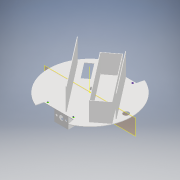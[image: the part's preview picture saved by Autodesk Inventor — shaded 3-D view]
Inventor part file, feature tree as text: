
AUTODESK INVENTOR PART (.ipt)
format: ipt  version: 2020 (Build 240168000, 168)  size: 422,400 bytes
history: native  units: mm
features: sketch x20, extrude x16, reference x13, other x3, fillet x3, projected_geometry x2, plane x1, mirror x1
ambient origin geometry x8: Origin, YZ Plane, XZ Plane, XY Plane, X Axis, Y Axis, Z Axis, Center Point
bodies: Solid1 (feature_tree)
feature tree (59):
  extrude  "Extrusion1"  Depth=1.0mm TaperAngle=0.0deg
  sketch  "Sketch2"  dims[d5=1.0mm d6=0.0mm d29=12.5mm]
  extrude  "Extrusion2"  Depth=12.5mm
  extrude  "Extrusion6"  Depth=1.0mm
  extrude  "Extrusion7"  Depth=25.0mm
  extrude  "Extrusion8"  Depth=1.0mm TaperAngle=0.0deg
  plane  "Work Plane1"
  mirror  "Mirror1"
  extrude  "Extrusion9"  Depth=1.0mm
  extrude  "Extrusion10"  Depth=40.0mm TaperAngle=0.0deg
  extrude  "Extrusion11"  Depth=24.0mm
  extrude  "Extrusion13"  Depth=34.0mm TaperAngle=0.0deg
  other  "Work Axis1"
  extrude  "Extrusion15"  Depth=4.0mm TaperAngle=0.0deg
  fillet  "Fillet2"  Radius=1.0mm
  extrude  "Extrusion21"  Depth=1.0mm TaperAngle=0.0deg
  extrude  "Extrusion24"  Depth=1.0mm
  extrude  "Extrusion25"  Depth=1.0mm
  sketch  "Sketch30"  dims[d105=2.0mm d106=1.0mm d107=0.0mm]
  sketch  "Sketch31"  dims[d111=1.0mm d112=0.0mm d113=2.0mm d114=1.0mm d115=0.0mm]
  extrude  "Extrusion27"  Depth=40.0mm TaperAngle=0.0deg
  fillet  "Fillet6"  Radius=40.0mm
  extrude  "Extrusion28"  Depth=1.0mm TaperAngle=0.0deg
  extrude  "Extrusion29"  Depth=2.0mm
  fillet  "Fillet7"  Radius=1.0mm
  sketch  "Sketch37"  dims[d18=0.872665mm d19=0.5mm d20=0.872665mm d21=0.872665mm d26=0.5mm d27=0.872665mm d28=0.5mm d108=0.5mm d109=0.872665mm d110=0.5mm]
  sketch  "Sketch1"  dims[d0=150.0mm d1=1.0mm d2=0.0mm]
  sketch  "Sketch3"  dims[d30=12.5mm d31=1.0mm]
  sketch  "Sketch8"  dims[d32=25.0mm d33=0.0mm d35=8.0mm]
  sketch  "Sketch9"  dims[d37=3.5mm d38=1.0mm d39=0.0mm]
  sketch  "Sketch10"  dims[d41=1.0mm d42=1.0mm]
  sketch  "Sketch11"  dims[d43=20.6mm d44=40.0mm d45=0.0mm]
  sketch  "Sketch12"  dims[d46=106.0mm d47=24.0mm]
  projected_geometry  "Projected Loop4"
  sketch  "Sketch13"  dims[d48=1.0mm d53=34.0mm d54=0.0mm]
  projected_geometry  "Projected Loop5"
  sketch  "Sketch15"  dims[d55=4.0mm d56=0.0mm d57=4.0mm d58=0.0mm d62=1.0mm d63=0.0mm]
  reference  "Reference1"
  reference  "Reference2"
  reference  "Reference3"
  reference  "Reference4"
  reference  "Reference5"
  sketch  "Sketch17"  dims[d71=10.0mm d72=1.0mm d73=0.0mm]
  sketch  "Sketch25"  dims[d85=5.0mm d91=1.0mm]
  sketch  "Sketch28"  dims[d92=40.0mm d93=0.0mm d100=1.0mm]
  sketch  "Sketch29"  dims[d101=1.0mm d102=40.0mm d103=0.0mm d104=40.0mm]
  sketch  "Sketch33"  dims[d116=1.0mm d117=0.0mm]
  reference  "Reference12"
  reference  "Reference13"
  reference  "Reference14"
  sketch  "Sketch34"  dims[d118=2.0mm]
  reference  "Reference15"
  reference  "Reference16"
  reference  "Reference17"
  reference  "Reference18"
  reference  "Reference19"
  sketch  "Sketch35"  dims[d17=0.5mm]
  other  "Assembly_for_print.iam"
  other  "DropMechanism_v.2.0:1"
